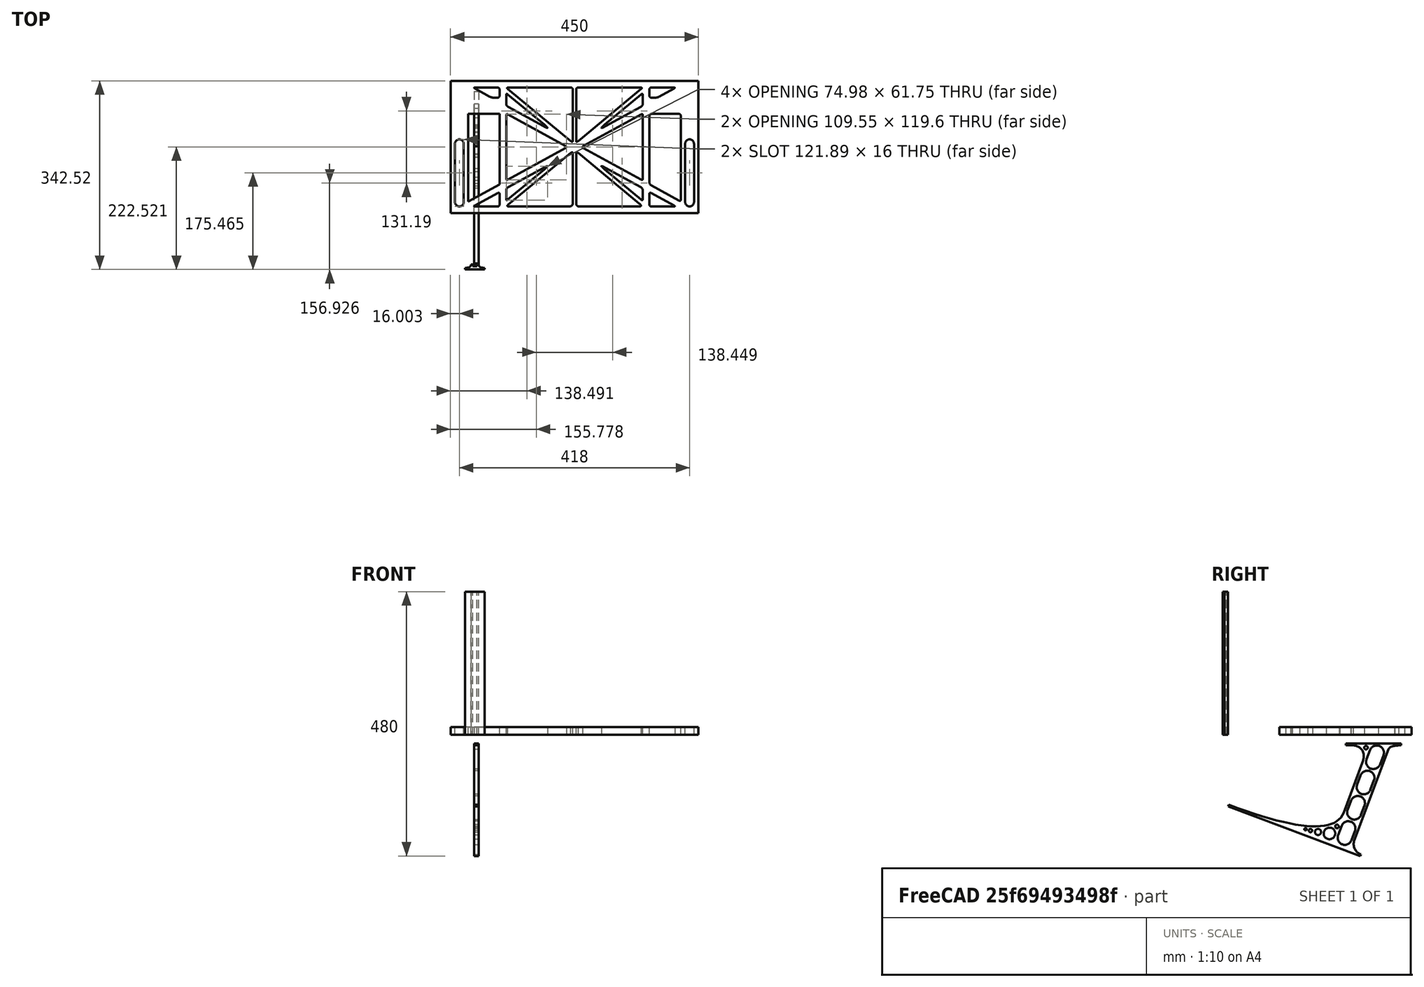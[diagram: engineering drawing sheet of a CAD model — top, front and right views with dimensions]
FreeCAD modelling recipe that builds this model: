
FCSTD DOCUMENT  (FreeCAD 0.19R0.19.2)
Label: laptopStand138FCStd
License: All rights reserved
LicenseURL: http://en.wikipedia.org/wiki/All_rights_reserved
objects: Sketcher::SketchObject×3, Part::Extrusion×3
note: 6 computed .brp shape members not serialized (recipe doc carries the construction recipe); baked Part::Feature solids carry a one-line shape summary decoded from their .brp

FEATURE [Sketcher::SketchObject] Sketch
  FullyConstrained = false
  sketch-geometry (349):
    g0: LineSegment StartX=-10.9272 StartY=-82.7794 StartZ=0 EndX=46.0728 EndY=-51.4823 EndZ=0
    g1: LineSegment StartX=-10.9272 StartY=76.4095 StartZ=0 EndX=-10.9272 EndY=-82.7794 EndZ=0
    g2: LineSegment StartX=46.0728 StartY=76.4095 StartZ=0 EndX=46.0728 EndY=-51.4823 EndZ=0
    g3: LineSegment StartX=-42.9272 StartY=136.221 StartZ=0 EndX=-42.9272 EndY=-103.779 EndZ=0
    g4: LineSegment StartX=407.073 StartY=136.221 StartZ=0 EndX=407.073 EndY=-103.779 EndZ=0
    g5: ArcOfCircle CenterX=-26.9272 CenterY=-83.7794 CenterZ=0 NormalX=0 NormalY=0 NormalZ=1 AngleXU=0 Radius=8 StartAngle=3.14159 EndAngle=6.28319
    g6: ArcOfCircle CenterX=391.073 CenterY=22.1087 CenterZ=0 NormalX=0 NormalY=0 NormalZ=1 AngleXU=0 Radius=8 StartAngle=-4.4e-15 EndAngle=3.14159
    g7: LineSegment StartX=399.073 StartY=22.1087 StartZ=0 EndX=399.073 EndY=-83.7794 EndZ=0
    g8: LineSegment StartX=383.073 StartY=22.1087 StartZ=0 EndX=383.073 EndY=-83.7794 EndZ=0
    g9: ArcOfCircle CenterX=391.073 CenterY=-83.7794 CenterZ=0 NormalX=0 NormalY=0 NormalZ=1 AngleXU=0 Radius=8 StartAngle=3.14159 EndAngle=6.28319
    g10: Circle CenterX=175.022 CenterY=27.0628 CenterZ=0 NormalX=0 NormalY=0 NormalZ=1 AngleXU=0 Radius=1
    g11: Circle CenterX=179.022 CenterY=24.8665 CenterZ=0 NormalX=0 NormalY=0 NormalZ=1 AngleXU=0 Radius=1
    g12: Circle CenterX=179.022 CenterY=27.0628 CenterZ=0 NormalX=0 NormalY=0 NormalZ=1 AngleXU=0 Radius=1
    g13: BSplineCurve PolesCount=3 KnotsCount=2 Degree=2 IsPeriodic=0
    g14: GeomPoint X=175.022 Y=27.0628 Z=0
    g15: GeomPoint X=179.022 Y=27.0628 Z=0
    g16: Circle CenterX=189.124 CenterY=27.0628 CenterZ=0 NormalX=0 NormalY=0 NormalZ=1 AngleXU=0 Radius=1
    g17: Circle CenterX=185.124 CenterY=24.8665 CenterZ=0 NormalX=0 NormalY=0 NormalZ=1 AngleXU=0 Radius=1
    g18: Circle CenterX=185.124 CenterY=27.0628 CenterZ=0 NormalX=0 NormalY=0 NormalZ=1 AngleXU=0 Radius=1
    g19: BSplineCurve PolesCount=3 KnotsCount=2 Degree=2 IsPeriodic=0
    g20: GeomPoint X=189.124 Y=27.0628 Z=0
    g21: GeomPoint X=185.124 Y=27.0628 Z=0
    g22: Circle CenterX=175.022 CenterY=5.37834 CenterZ=0 NormalX=0 NormalY=0 NormalZ=1 AngleXU=0 Radius=1
    g23: Circle CenterX=179.022 CenterY=7.57463 CenterZ=0 NormalX=0 NormalY=0 NormalZ=1 AngleXU=0 Radius=1
    g24: Circle CenterX=179.022 CenterY=5.34704 CenterZ=0 NormalX=0 NormalY=0 NormalZ=1 AngleXU=0 Radius=1
    g25: BSplineCurve PolesCount=3 KnotsCount=2 Degree=2 IsPeriodic=0
    g26: GeomPoint X=175.022 Y=5.37834 Z=0
    g27: GeomPoint X=179.022 Y=5.34704 Z=0
    g28: Circle CenterX=189.124 CenterY=5.37834 CenterZ=0 NormalX=0 NormalY=0 NormalZ=1 AngleXU=0 Radius=1
    g29: Circle CenterX=185.124 CenterY=7.57463 CenterZ=0 NormalX=0 NormalY=0 NormalZ=1 AngleXU=0 Radius=1
    g30: Circle CenterX=185.124 CenterY=5.34704 CenterZ=0 NormalX=0 NormalY=0 NormalZ=1 AngleXU=0 Radius=1
    g31: BSplineCurve PolesCount=3 KnotsCount=2 Degree=2 IsPeriodic=0
    g32: GeomPoint X=189.124 Y=5.37834 Z=0
    g33: GeomPoint X=185.124 Y=5.34704 Z=0
    g34: Circle CenterX=165.871 CenterY=18.1458 CenterZ=0 NormalX=0 NormalY=0 NormalZ=1 AngleXU=0 Radius=1
    g35: Circle CenterX=169.377 CenterY=16.2206 CenterZ=0 NormalX=0 NormalY=0 NormalZ=1 AngleXU=0 Radius=1
    g36: Circle CenterX=165.871 CenterY=14.2954 CenterZ=0 NormalX=0 NormalY=0 NormalZ=1 AngleXU=0 Radius=1
    g37: BSplineCurve PolesCount=3 KnotsCount=2 Degree=2 IsPeriodic=0
    g38: GeomPoint X=165.871 Y=18.1458 Z=0
    g39: GeomPoint X=165.871 Y=14.2954 Z=0
    g40: Circle CenterX=198.275 CenterY=18.1458 CenterZ=0 NormalX=0 NormalY=0 NormalZ=1 AngleXU=0 Radius=1
    g41: Circle CenterX=194.768 CenterY=16.2206 CenterZ=0 NormalX=0 NormalY=0 NormalZ=1 AngleXU=0 Radius=1
    g42: Circle CenterX=198.275 CenterY=14.2954 CenterZ=0 NormalX=0 NormalY=0 NormalZ=1 AngleXU=0 Radius=1
    g43: BSplineCurve PolesCount=3 KnotsCount=2 Degree=2 IsPeriodic=0
    g44: GeomPoint X=198.275 Y=18.1458 Z=0
    g45: GeomPoint X=198.275 Y=14.2954 Z=0
    g46: LineSegment StartX=407.073 StartY=-103.779 StartZ=0 EndX=-42.9272 EndY=-103.779 EndZ=0
    g47: LineSegment StartX=407.073 StartY=136.221 StartZ=0 EndX=-42.9272 EndY=136.221 EndZ=0
    g48: LineSegment StartX=46.0728 StartY=76.4095 StartZ=0 EndX=-10.9272 EndY=76.4095 EndZ=0
    g49: Circle CenterX=125.607 CenterY=54.1951 CenterZ=0 NormalX=0 NormalY=0 NormalZ=1 AngleXU=0 Radius=1
    g50: Circle CenterX=139.632 CenterY=46.4944 CenterZ=0 NormalX=0 NormalY=0 NormalZ=1 AngleXU=0 Radius=1
    g51: Circle CenterX=127.326 CenterY=56.7187 CenterZ=0 NormalX=0 NormalY=0 NormalZ=1 AngleXU=0 Radius=1
    g52: BSplineCurve PolesCount=3 KnotsCount=2 Degree=2 IsPeriodic=0
    g53: GeomPoint X=125.607 Y=54.1951 Z=0
    g54: GeomPoint X=127.326 Y=56.7187 Z=0
    g55: Circle CenterX=236.821 CenterY=56.7187 CenterZ=0 NormalX=0 NormalY=0 NormalZ=1 AngleXU=0 Radius=1
    g56: Circle CenterX=224.513 CenterY=46.4944 CenterZ=0 NormalX=0 NormalY=0 NormalZ=1 AngleXU=0 Radius=1
    g57: Circle CenterX=238.538 CenterY=54.1951 CenterZ=0 NormalX=0 NormalY=0 NormalZ=1 AngleXU=0 Radius=1
    g58: BSplineCurve PolesCount=3 KnotsCount=2 Degree=2 IsPeriodic=0
    g59: GeomPoint X=236.821 Y=56.7187 Z=0
    g60: GeomPoint X=238.538 Y=54.1951 Z=0
    g61: Circle CenterX=238.538 CenterY=-21.7539 CenterZ=0 NormalX=0 NormalY=0 NormalZ=1 AngleXU=0 Radius=1
    g62: Circle CenterX=224.513 CenterY=-14.0532 CenterZ=0 NormalX=0 NormalY=0 NormalZ=1 AngleXU=0 Radius=1
    g63: Circle CenterX=236.821 CenterY=-24.2775 CenterZ=0 NormalX=0 NormalY=0 NormalZ=1 AngleXU=0 Radius=1
    g64: BSplineCurve PolesCount=3 KnotsCount=2 Degree=2 IsPeriodic=0
    g65: GeomPoint X=238.538 Y=-21.7539 Z=0
    g66: GeomPoint X=236.821 Y=-24.2775 Z=0
    g67: Circle CenterX=125.607 CenterY=-21.7539 CenterZ=0 NormalX=0 NormalY=0 NormalZ=1 AngleXU=0 Radius=1
    g68: Circle CenterX=139.632 CenterY=-14.0532 CenterZ=0 NormalX=0 NormalY=0 NormalZ=1 AngleXU=0 Radius=1
    g69: Circle CenterX=127.325 CenterY=-24.2775 CenterZ=0 NormalX=0 NormalY=0 NormalZ=1 AngleXU=0 Radius=1
    g70: BSplineCurve PolesCount=3 KnotsCount=2 Degree=2 IsPeriodic=0
    g71: GeomPoint X=125.607 Y=-21.7539 Z=0
    g72: GeomPoint X=127.325 Y=-24.2775 Z=0
    g73: Circle CenterX=302.996 CenterY=111.695 CenterZ=0 NormalX=0 NormalY=0 NormalZ=1 AngleXU=0 Radius=1
    g74: Circle CenterX=306.073 CenterY=114.251 CenterZ=0 NormalX=0 NormalY=0 NormalZ=1 AngleXU=0 Radius=1
    g75: Circle CenterX=306.073 CenterY=110.251 CenterZ=0 NormalX=0 NormalY=0 NormalZ=1 AngleXU=0 Radius=1
    g76: BSplineCurve PolesCount=3 KnotsCount=2 Degree=2 IsPeriodic=0
    g77: GeomPoint X=302.996 Y=111.695 Z=0
    g78: GeomPoint X=306.073 Y=110.251 Z=0
    g79: Circle CenterX=306.073 CenterY=95.2763 CenterZ=0 NormalX=0 NormalY=0 NormalZ=1 AngleXU=0 Radius=1
    g80: Circle CenterX=306.073 CenterY=91.2763 CenterZ=0 NormalX=0 NormalY=0 NormalZ=1 AngleXU=0 Radius=1
    g81: Circle CenterX=302.567 CenterY=89.3511 CenterZ=0 NormalX=0 NormalY=0 NormalZ=1 AngleXU=0 Radius=1
    g82: BSplineCurve PolesCount=3 KnotsCount=2 Degree=2 IsPeriodic=0
    g83: GeomPoint X=306.073 Y=95.2763 Z=0
    g84: GeomPoint X=302.567 Y=89.3511 Z=0
    g85: LineSegment StartX=306.073 StartY=110.251 StartZ=0 EndX=306.073 EndY=95.2763 EndZ=0
    g86: LineSegment StartX=302.996 StartY=111.695 StartZ=0 EndX=236.821 EndY=56.7187 EndZ=0
    g87: LineSegment StartX=238.538 StartY=54.1951 StartZ=0 EndX=302.567 EndY=89.3511 EndZ=0
    g88: Circle CenterX=61.1496 CenterY=111.695 CenterZ=0 NormalX=0 NormalY=0 NormalZ=1 AngleXU=0 Radius=1
    g89: Circle CenterX=58.0728 CenterY=114.251 CenterZ=0 NormalX=0 NormalY=0 NormalZ=1 AngleXU=0 Radius=1
    g90: Circle CenterX=58.0728 CenterY=110.251 CenterZ=0 NormalX=0 NormalY=0 NormalZ=1 AngleXU=0 Radius=1
    g91: BSplineCurve PolesCount=3 KnotsCount=2 Degree=2 IsPeriodic=0
    g92: GeomPoint X=61.1496 Y=111.695 Z=0
    g93: GeomPoint X=58.0728 Y=110.251 Z=0
    g94: Circle CenterX=61.5791 CenterY=89.3511 CenterZ=0 NormalX=0 NormalY=0 NormalZ=1 AngleXU=0 Radius=1
    g95: Circle CenterX=58.0728 CenterY=91.2763 CenterZ=0 NormalX=0 NormalY=0 NormalZ=1 AngleXU=0 Radius=1
    g96: Circle CenterX=58.0728 CenterY=95.2763 CenterZ=0 NormalX=0 NormalY=0 NormalZ=1 AngleXU=0 Radius=1
    g97: BSplineCurve PolesCount=3 KnotsCount=2 Degree=2 IsPeriodic=0
    g98: GeomPoint X=61.5791 Y=89.3511 Z=0
    g99: GeomPoint X=58.0728 Y=95.2763 Z=0
    g100: LineSegment StartX=58.0728 StartY=110.251 StartZ=0 EndX=58.0728 EndY=95.2763 EndZ=0
    g101: LineSegment StartX=61.1496 StartY=111.695 StartZ=0 EndX=127.326 EndY=56.7187 EndZ=0
    g102: LineSegment StartX=125.607 StartY=54.1951 StartZ=0 EndX=61.5791 EndY=89.3511 EndZ=0
    g103: Circle CenterX=61.5791 CenterY=-56.9099 CenterZ=0 NormalX=0 NormalY=0 NormalZ=1 AngleXU=0 Radius=1
    g104: Circle CenterX=58.0728 CenterY=-58.8351 CenterZ=0 NormalX=0 NormalY=0 NormalZ=1 AngleXU=0 Radius=1
    g105: Circle CenterX=58.0728 CenterY=-62.8351 CenterZ=0 NormalX=0 NormalY=0 NormalZ=1 AngleXU=0 Radius=1
    g106: BSplineCurve PolesCount=3 KnotsCount=2 Degree=2 IsPeriodic=0
    g107: GeomPoint X=61.5791 Y=-56.9099 Z=0
    g108: GeomPoint X=58.0728 Y=-62.8351 Z=0
    g109: Circle CenterX=58.0728 CenterY=-77.8102 CenterZ=0 NormalX=0 NormalY=0 NormalZ=1 AngleXU=0 Radius=1
    g110: Circle CenterX=58.0728 CenterY=-81.8102 CenterZ=0 NormalX=0 NormalY=0 NormalZ=1 AngleXU=0 Radius=1
    g111: Circle CenterX=61.1496 CenterY=-79.2541 CenterZ=0 NormalX=0 NormalY=0 NormalZ=1 AngleXU=0 Radius=1
    g112: BSplineCurve PolesCount=3 KnotsCount=2 Degree=2 IsPeriodic=0
    g113: GeomPoint X=58.0728 Y=-77.8102 Z=0
    g114: GeomPoint X=61.1496 Y=-79.2541 Z=0
    g115: LineSegment StartX=58.0728 StartY=-62.8351 StartZ=0 EndX=58.0728 EndY=-77.8102 EndZ=0
    g116: LineSegment StartX=61.1496 StartY=-79.2541 StartZ=0 EndX=127.325 EndY=-24.2775 EndZ=0
    g117: LineSegment StartX=125.607 StartY=-21.7539 StartZ=0 EndX=61.5791 EndY=-56.9099 EndZ=0
    g118: Circle CenterX=302.567 CenterY=-56.9099 CenterZ=0 NormalX=0 NormalY=0 NormalZ=1 AngleXU=0 Radius=1
    g119: Circle CenterX=306.073 CenterY=-58.8351 CenterZ=0 NormalX=0 NormalY=0 NormalZ=1 AngleXU=0 Radius=1
    g120: Circle CenterX=306.073 CenterY=-62.8351 CenterZ=0 NormalX=0 NormalY=0 NormalZ=1 AngleXU=0 Radius=1
    g121: BSplineCurve PolesCount=3 KnotsCount=2 Degree=2 IsPeriodic=0
    g122: GeomPoint X=302.567 Y=-56.9099 Z=0
    g123: GeomPoint X=306.073 Y=-62.8351 Z=0
    g124: Circle CenterX=302.996 CenterY=-79.2541 CenterZ=0 NormalX=0 NormalY=0 NormalZ=1 AngleXU=0 Radius=1
    g125: Circle CenterX=306.073 CenterY=-81.8102 CenterZ=0 NormalX=0 NormalY=0 NormalZ=1 AngleXU=0 Radius=1
    g126: Circle CenterX=306.073 CenterY=-77.8102 CenterZ=0 NormalX=0 NormalY=0 NormalZ=1 AngleXU=0 Radius=1
    g127: BSplineCurve PolesCount=3 KnotsCount=2 Degree=2 IsPeriodic=0
    g128: GeomPoint X=302.996 Y=-79.2541 Z=0
    g129: GeomPoint X=306.073 Y=-77.8102 Z=0
    g130: LineSegment StartX=306.073 StartY=-62.8351 StartZ=0 EndX=306.073 EndY=-77.8102 EndZ=0
    g131: LineSegment StartX=302.996 StartY=-79.2541 StartZ=0 EndX=236.821 EndY=-24.2775 EndZ=0
    g132: LineSegment StartX=238.538 StartY=-21.7539 StartZ=0 EndX=302.567 EndY=-56.9099 EndZ=0
    g133: Circle CenterX=61.6457 CenterY=-88.8112 CenterZ=0 NormalX=0 NormalY=0 NormalZ=1 AngleXU=0 Radius=1
    g134: Circle CenterX=58.0728 CenterY=-91.7794 CenterZ=0 NormalX=0 NormalY=0 NormalZ=1 AngleXU=0 Radius=1
    g135: Circle CenterX=63.9135 CenterY=-91.7794 CenterZ=0 NormalX=0 NormalY=0 NormalZ=1 AngleXU=0 Radius=1
    g136: BSplineCurve PolesCount=3 KnotsCount=2 Degree=2 IsPeriodic=0
    g137: GeomPoint X=61.6457 Y=-88.8112 Z=0
    g138: GeomPoint X=63.9135 Y=-91.7794 Z=0
    g139: Circle CenterX=179.022 CenterY=-85.8163 CenterZ=0 NormalX=0 NormalY=0 NormalZ=1 AngleXU=0 Radius=1
    g140: Circle CenterX=179.022 CenterY=-91.7794 CenterZ=0 NormalX=0 NormalY=0 NormalZ=1 AngleXU=0 Radius=1
    g141: Circle CenterX=171.895 CenterY=-91.7794 CenterZ=0 NormalX=0 NormalY=0 NormalZ=1 AngleXU=0 Radius=1
    g142: BSplineCurve PolesCount=3 KnotsCount=2 Degree=2 IsPeriodic=0
    g143: GeomPoint X=179.022 Y=-85.8163 Z=0
    g144: GeomPoint X=171.895 Y=-91.7794 Z=0
    g145: Circle CenterX=185.124 CenterY=-86.2028 CenterZ=0 NormalX=0 NormalY=0 NormalZ=1 AngleXU=0 Radius=1
    g146: Circle CenterX=185.124 CenterY=-91.7794 CenterZ=0 NormalX=0 NormalY=0 NormalZ=1 AngleXU=0 Radius=1
    g147: Circle CenterX=191.747 CenterY=-91.7794 CenterZ=0 NormalX=0 NormalY=0 NormalZ=1 AngleXU=0 Radius=1
    g148: BSplineCurve PolesCount=3 KnotsCount=2 Degree=2 IsPeriodic=0
    g149: GeomPoint X=185.124 Y=-86.2028 Z=0
    g150: GeomPoint X=191.747 Y=-91.7794 Z=0
    g151: Circle CenterX=299.888 CenterY=-86.6413 CenterZ=0 NormalX=0 NormalY=0 NormalZ=1 AngleXU=0 Radius=1
    g152: Circle CenterX=306.073 CenterY=-91.7794 CenterZ=0 NormalX=0 NormalY=0 NormalZ=1 AngleXU=0 Radius=1
    g153: Circle CenterX=298.776 CenterY=-91.7794 CenterZ=0 NormalX=0 NormalY=0 NormalZ=1 AngleXU=0 Radius=1
    g154: BSplineCurve PolesCount=3 KnotsCount=2 Degree=2 IsPeriodic=0
    g155: GeomPoint X=299.888 Y=-86.6413 Z=0
    g156: GeomPoint X=298.776 Y=-91.7794 Z=0
    g157: LineSegment StartX=189.124 StartY=5.37834 StartZ=0 EndX=299.888 EndY=-86.6413 EndZ=0
    g158: LineSegment StartX=298.776 StartY=-91.7794 StartZ=0 EndX=191.747 EndY=-91.7794 EndZ=0
    g159: LineSegment StartX=185.124 StartY=-86.2028 StartZ=0 EndX=185.124 EndY=5.34704 EndZ=0
    g160: LineSegment StartX=179.022 StartY=5.34704 StartZ=0 EndX=179.022 EndY=-85.8163 EndZ=0
    g161: LineSegment StartX=171.895 StartY=-91.7794 StartZ=0 EndX=63.9135 EndY=-91.7794 EndZ=0
    g162: LineSegment StartX=61.6457 StartY=-88.8112 StartZ=0 EndX=175.022 EndY=5.37834 EndZ=0
    g163: Circle CenterX=302.073 CenterY=124.221 CenterZ=0 NormalX=0 NormalY=0 NormalZ=1 AngleXU=0 Radius=1
    g164: Circle CenterX=306.073 CenterY=124.221 CenterZ=0 NormalX=0 NormalY=0 NormalZ=1 AngleXU=0 Radius=1
    g165: Circle CenterX=302.996 CenterY=121.665 CenterZ=0 NormalX=0 NormalY=0 NormalZ=1 AngleXU=0 Radius=1
    g166: BSplineCurve PolesCount=3 KnotsCount=2 Degree=2 IsPeriodic=0
    g167: GeomPoint X=302.073 Y=124.221 Z=0
    g168: GeomPoint X=302.996 Y=121.665 Z=0
    g169: Circle CenterX=189.124 CenterY=124.221 CenterZ=0 NormalX=0 NormalY=0 NormalZ=1 AngleXU=0 Radius=1
    g170: Circle CenterX=185.124 CenterY=124.221 CenterZ=0 NormalX=0 NormalY=0 NormalZ=1 AngleXU=0 Radius=1
    g171: Circle CenterX=185.124 CenterY=120.221 CenterZ=0 NormalX=0 NormalY=0 NormalZ=1 AngleXU=0 Radius=1
    g172: BSplineCurve PolesCount=3 KnotsCount=2 Degree=2 IsPeriodic=0
    g173: GeomPoint X=189.124 Y=124.221 Z=0
    g174: GeomPoint X=185.124 Y=120.221 Z=0
    g175: Circle CenterX=175.022 CenterY=124.221 CenterZ=0 NormalX=0 NormalY=0 NormalZ=1 AngleXU=0 Radius=1
    g176: Circle CenterX=179.022 CenterY=124.221 CenterZ=0 NormalX=0 NormalY=0 NormalZ=1 AngleXU=0 Radius=1
    g177: Circle CenterX=179.022 CenterY=120.221 CenterZ=0 NormalX=0 NormalY=0 NormalZ=1 AngleXU=0 Radius=1
    g178: BSplineCurve PolesCount=3 KnotsCount=2 Degree=2 IsPeriodic=0
    g179: GeomPoint X=175.022 Y=124.221 Z=0
    g180: GeomPoint X=179.022 Y=120.221 Z=0
    g181: Circle CenterX=62.0728 CenterY=124.221 CenterZ=0 NormalX=0 NormalY=0 NormalZ=1 AngleXU=0 Radius=1
    g182: Circle CenterX=58.0728 CenterY=124.221 CenterZ=0 NormalX=0 NormalY=0 NormalZ=1 AngleXU=0 Radius=1
    g183: Circle CenterX=61.1496 CenterY=121.665 CenterZ=0 NormalX=0 NormalY=0 NormalZ=1 AngleXU=0 Radius=1
    g184: BSplineCurve PolesCount=3 KnotsCount=2 Degree=2 IsPeriodic=0
    g185: GeomPoint X=62.0728 Y=124.221 Z=0
    g186: GeomPoint X=61.1496 Y=121.665 Z=0
    g187: LineSegment StartX=62.0728 StartY=124.221 StartZ=0 EndX=175.022 EndY=124.221 EndZ=0
    g188: LineSegment StartX=179.022 StartY=120.221 StartZ=0 EndX=179.022 EndY=27.0628 EndZ=0
    g189: LineSegment StartX=185.124 StartY=27.0628 StartZ=0 EndX=185.124 EndY=120.221 EndZ=0
    g190: LineSegment StartX=189.124 StartY=124.221 StartZ=0 EndX=302.073 EndY=124.221 EndZ=0
    g191: LineSegment StartX=302.996 StartY=121.665 StartZ=0 EndX=189.124 EndY=27.0628 EndZ=0
    g192: LineSegment StartX=175.022 StartY=27.0628 StartZ=0 EndX=61.1496 EndY=121.665 EndZ=0
    g193: Circle CenterX=61.5791 CenterY=75.4095 CenterZ=0 NormalX=0 NormalY=0 NormalZ=1 AngleXU=0 Radius=1
    g194: Circle CenterX=58.0728 CenterY=77.3346 CenterZ=0 NormalX=0 NormalY=0 NormalZ=1 AngleXU=0 Radius=1
    g195: Circle CenterX=58.0728 CenterY=73.3346 CenterZ=0 NormalX=0 NormalY=0 NormalZ=1 AngleXU=0 Radius=1
    g196: BSplineCurve PolesCount=3 KnotsCount=2 Degree=2 IsPeriodic=0
    g197: GeomPoint X=61.5791 Y=75.4095 Z=0
    g198: GeomPoint X=58.0728 Y=73.3346 Z=0
    g199: Circle CenterX=58.0728 CenterY=-40.8935 CenterZ=0 NormalX=0 NormalY=0 NormalZ=1 AngleXU=0 Radius=1
    g200: Circle CenterX=58.0728 CenterY=-44.8935 CenterZ=0 NormalX=0 NormalY=0 NormalZ=1 AngleXU=0 Radius=1
    g201: Circle CenterX=61.5791 CenterY=-42.9683 CenterZ=0 NormalX=0 NormalY=0 NormalZ=1 AngleXU=0 Radius=1
    g202: BSplineCurve PolesCount=3 KnotsCount=2 Degree=2 IsPeriodic=0
    g203: GeomPoint X=58.0728 Y=-40.8935 Z=0
    g204: GeomPoint X=61.5791 Y=-42.9683 Z=0
    g205: LineSegment StartX=61.5791 StartY=-42.9683 StartZ=0 EndX=165.871 EndY=14.2954 EndZ=0
    g206: LineSegment StartX=165.871 StartY=18.1458 StartZ=0 EndX=61.5791 EndY=75.4095 EndZ=0
    g207: LineSegment StartX=58.0728 StartY=73.3346 StartZ=0 EndX=58.0728 EndY=-40.8935 EndZ=0
    g208: Circle CenterX=302.567 CenterY=-42.9683 CenterZ=0 NormalX=0 NormalY=0 NormalZ=1 AngleXU=0 Radius=1
    g209: Circle CenterX=306.073 CenterY=-44.8935 CenterZ=0 NormalX=0 NormalY=0 NormalZ=1 AngleXU=0 Radius=1
    g210: Circle CenterX=306.073 CenterY=-40.8935 CenterZ=0 NormalX=0 NormalY=0 NormalZ=1 AngleXU=0 Radius=1
    g211: BSplineCurve PolesCount=3 KnotsCount=2 Degree=2 IsPeriodic=0
    g212: GeomPoint X=302.567 Y=-42.9683 Z=0
    g213: GeomPoint X=306.073 Y=-40.8935 Z=0
    g214: Circle CenterX=306.073 CenterY=73.3346 CenterZ=0 NormalX=0 NormalY=0 NormalZ=1 AngleXU=0 Radius=1
    g215: Circle CenterX=306.073 CenterY=77.3346 CenterZ=0 NormalX=0 NormalY=0 NormalZ=1 AngleXU=0 Radius=1
    g216: Circle CenterX=302.567 CenterY=75.4095 CenterZ=0 NormalX=0 NormalY=0 NormalZ=1 AngleXU=0 Radius=1
    g217: BSplineCurve PolesCount=3 KnotsCount=2 Degree=2 IsPeriodic=0
    g218: GeomPoint X=306.073 Y=73.3346 Z=0
    g219: GeomPoint X=302.567 Y=75.4095 Z=0
    g220: LineSegment StartX=302.567 StartY=-42.9683 StartZ=0 EndX=198.275 EndY=14.2954 EndZ=0
    g221: LineSegment StartX=198.275 StartY=18.1458 StartZ=0 EndX=302.567 EndY=75.4095 EndZ=0
    g222: LineSegment StartX=306.073 StartY=73.3346 StartZ=0 EndX=306.073 EndY=-40.8935 EndZ=0
    g223: LineSegment StartX=322.073 StartY=105.865 StartZ=0 EndX=328.643 EndY=105.865 EndZ=0
    g224: LineSegment StartX=318.073 StartY=120.221 StartZ=0 EndX=318.073 EndY=109.865 EndZ=0
    g225: LineSegment StartX=336.157 StartY=107.779 StartZ=0 EndX=362.567 EndY=122.294 EndZ=0
    g226: Circle CenterX=362.073 CenterY=124.221 CenterZ=0 NormalX=0 NormalY=0 NormalZ=1 AngleXU=0 Radius=1
    g227: Circle CenterX=366.073 CenterY=124.221 CenterZ=0 NormalX=0 NormalY=0 NormalZ=1 AngleXU=0 Radius=1
    g228: Circle CenterX=362.567 CenterY=122.294 CenterZ=0 NormalX=0 NormalY=0 NormalZ=1 AngleXU=0 Radius=1
    g229: BSplineCurve PolesCount=3 KnotsCount=2 Degree=2 IsPeriodic=0
    g230: GeomPoint X=362.073 Y=124.221 Z=0
    g231: GeomPoint X=362.567 Y=122.294 Z=0
    g232: Circle CenterX=322.073 CenterY=124.221 CenterZ=0 NormalX=0 NormalY=0 NormalZ=1 AngleXU=0 Radius=1
    g233: Circle CenterX=318.073 CenterY=124.221 CenterZ=0 NormalX=0 NormalY=0 NormalZ=1 AngleXU=0 Radius=1
    g234: Circle CenterX=318.073 CenterY=120.221 CenterZ=0 NormalX=0 NormalY=0 NormalZ=1 AngleXU=0 Radius=1
    g235: BSplineCurve PolesCount=3 KnotsCount=2 Degree=2 IsPeriodic=0
    g236: GeomPoint X=322.073 Y=124.221 Z=0
    g237: GeomPoint X=318.073 Y=120.221 Z=0
    g238: Circle CenterX=322.073 CenterY=105.865 CenterZ=0 NormalX=0 NormalY=0 NormalZ=1 AngleXU=0 Radius=1
    g239: Circle CenterX=318.073 CenterY=105.865 CenterZ=0 NormalX=0 NormalY=0 NormalZ=1 AngleXU=0 Radius=1
    g240: Circle CenterX=318.073 CenterY=109.865 CenterZ=0 NormalX=0 NormalY=0 NormalZ=1 AngleXU=0 Radius=1
    g241: BSplineCurve PolesCount=3 KnotsCount=2 Degree=2 IsPeriodic=0
    g242: GeomPoint X=322.073 Y=105.865 Z=0
    g243: GeomPoint X=318.073 Y=109.865 Z=0
    g244: Circle CenterX=336.157 CenterY=107.779 CenterZ=0 NormalX=0 NormalY=0 NormalZ=1 AngleXU=0 Radius=1
    g245: Circle CenterX=332.651 CenterY=105.853 CenterZ=0 NormalX=0 NormalY=0 NormalZ=1 AngleXU=0 Radius=1
    g246: Circle CenterX=328.643 CenterY=105.865 CenterZ=0 NormalX=0 NormalY=0 NormalZ=1 AngleXU=0 Radius=1
    g247: BSplineCurve PolesCount=3 KnotsCount=2 Degree=2 IsPeriodic=0
    g248: GeomPoint X=336.157 Y=107.779 Z=0
    g249: GeomPoint X=328.643 Y=105.865 Z=0
    g250: LineSegment StartX=322.073 StartY=124.221 StartZ=0 EndX=362.073 EndY=124.221 EndZ=0
    g251: Circle CenterX=371.567 CenterY=-80.8644 CenterZ=0 NormalX=0 NormalY=0 NormalZ=1 AngleXU=0 Radius=1
    g252: Circle CenterX=375.073 CenterY=-82.7896 CenterZ=0 NormalX=0 NormalY=0 NormalZ=1 AngleXU=0 Radius=1
    g253: Circle CenterX=375.073 CenterY=-78.7896 CenterZ=0 NormalX=0 NormalY=0 NormalZ=1 AngleXU=0 Radius=1
    g254: BSplineCurve PolesCount=3 KnotsCount=2 Degree=2 IsPeriodic=0
    g255: GeomPoint X=371.567 Y=-80.8644 Z=0
    g256: GeomPoint X=375.073 Y=-78.7896 Z=0
    g257: Circle CenterX=321.579 CenterY=-53.4075 CenterZ=0 NormalX=0 NormalY=0 NormalZ=1 AngleXU=0 Radius=1
    g258: Circle CenterX=318.073 CenterY=-51.4823 CenterZ=0 NormalX=0 NormalY=0 NormalZ=1 AngleXU=0 Radius=1
    g259: Circle CenterX=318.073 CenterY=-47.4805 CenterZ=0 NormalX=0 NormalY=0 NormalZ=1 AngleXU=0 Radius=1
    g260: BSplineCurve PolesCount=3 KnotsCount=2 Degree=2 IsPeriodic=0
    g261: GeomPoint X=321.579 Y=-53.4075 Z=0
    g262: GeomPoint X=318.073 Y=-47.4805 Z=0
    g263: LineSegment StartX=371.567 StartY=-80.8644 StartZ=0 EndX=321.579 EndY=-53.4075 EndZ=0
    g264: Circle CenterX=321.579 CenterY=-67.3492 CenterZ=0 NormalX=0 NormalY=0 NormalZ=1 AngleXU=0 Radius=1
    g265: Circle CenterX=318.073 CenterY=-65.424 CenterZ=0 NormalX=0 NormalY=0 NormalZ=1 AngleXU=0 Radius=1
    g266: Circle CenterX=318.073 CenterY=-69.424 CenterZ=0 NormalX=0 NormalY=0 NormalZ=1 AngleXU=0 Radius=1
    g267: BSplineCurve PolesCount=3 KnotsCount=2 Degree=2 IsPeriodic=0
    g268: GeomPoint X=321.579 Y=-67.3492 Z=0
    g269: GeomPoint X=318.073 Y=-69.424 Z=0
    g270: Circle CenterX=362.567 CenterY=-89.8542 CenterZ=0 NormalX=0 NormalY=0 NormalZ=1 AngleXU=0 Radius=1
    g271: Circle CenterX=366.073 CenterY=-91.7794 CenterZ=0 NormalX=0 NormalY=0 NormalZ=1 AngleXU=0 Radius=1
    g272: Circle CenterX=362.073 CenterY=-91.7794 CenterZ=0 NormalX=0 NormalY=0 NormalZ=1 AngleXU=0 Radius=1
    g273: BSplineCurve PolesCount=3 KnotsCount=2 Degree=2 IsPeriodic=0
    g274: GeomPoint X=362.567 Y=-89.8542 Z=0
    g275: GeomPoint X=362.073 Y=-91.7794 Z=0
    g276: Circle CenterX=322.073 CenterY=-91.7794 CenterZ=0 NormalX=0 NormalY=0 NormalZ=1 AngleXU=0 Radius=1
    g277: Circle CenterX=318.073 CenterY=-91.7794 CenterZ=0 NormalX=0 NormalY=0 NormalZ=1 AngleXU=0 Radius=1
    g278: Circle CenterX=318.073 CenterY=-87.7794 CenterZ=0 NormalX=0 NormalY=0 NormalZ=1 AngleXU=0 Radius=1
    g279: BSplineCurve PolesCount=3 KnotsCount=2 Degree=2 IsPeriodic=0
    g280: GeomPoint X=322.073 Y=-91.7794 Z=0
    g281: GeomPoint X=318.073 Y=-87.7794 Z=0
    g282: LineSegment StartX=362.567 StartY=-89.8542 StartZ=0 EndX=321.579 EndY=-67.3492 EndZ=0
    g283: LineSegment StartX=318.073 StartY=-69.424 StartZ=0 EndX=318.073 EndY=-87.7794 EndZ=0
    g284: LineSegment StartX=322.073 StartY=-91.7794 StartZ=0 EndX=362.073 EndY=-91.7794 EndZ=0
    g285: Circle CenterX=2.07281 CenterY=124.221 CenterZ=0 NormalX=0 NormalY=0 NormalZ=1 AngleXU=0 Radius=1
    g286: Circle CenterX=1.57905 CenterY=122.295 CenterZ=0 NormalX=0 NormalY=0 NormalZ=1 AngleXU=0 Radius=1
    g287: BSplineCurve PolesCount=3 KnotsCount=2 Degree=2 IsPeriodic=0
    g288: GeomPoint X=2.07281 Y=124.221 Z=0
    g289: GeomPoint X=1.57905 Y=122.295 Z=0
    g290: Circle CenterX=42.0728 CenterY=124.221 CenterZ=0 NormalX=0 NormalY=0 NormalZ=1 AngleXU=0 Radius=1
    g291: Circle CenterX=46.0728 CenterY=124.221 CenterZ=0 NormalX=0 NormalY=0 NormalZ=1 AngleXU=0 Radius=1
    g292: Circle CenterX=46.0728 CenterY=120.221 CenterZ=0 NormalX=0 NormalY=0 NormalZ=1 AngleXU=0 Radius=1
    g293: BSplineCurve PolesCount=3 KnotsCount=2 Degree=2 IsPeriodic=0
    g294: GeomPoint X=42.0728 Y=124.221 Z=0
    g295: GeomPoint X=46.0728 Y=120.221 Z=0
    g296: Circle CenterX=46.0728 CenterY=109.865 CenterZ=0 NormalX=0 NormalY=0 NormalZ=1 AngleXU=0 Radius=1
    g297: Circle CenterX=46.0728 CenterY=105.865 CenterZ=0 NormalX=0 NormalY=0 NormalZ=1 AngleXU=0 Radius=1
    g298: Circle CenterX=42.0728 CenterY=105.865 CenterZ=0 NormalX=0 NormalY=0 NormalZ=1 AngleXU=0 Radius=1
    g299: BSplineCurve PolesCount=3 KnotsCount=2 Degree=2 IsPeriodic=0
    g300: GeomPoint X=46.0728 Y=109.865 Z=0
    g301: GeomPoint X=42.0728 Y=105.865 Z=0
    g302: Circle CenterX=35.5028 CenterY=105.865 CenterZ=0 NormalX=0 NormalY=0 NormalZ=1 AngleXU=0 Radius=1
    g303: Circle CenterX=31.5028 CenterY=105.865 CenterZ=0 NormalX=0 NormalY=0 NormalZ=1 AngleXU=0 Radius=1
    g304: Circle CenterX=27.9965 CenterY=107.79 CenterZ=0 NormalX=0 NormalY=0 NormalZ=1 AngleXU=0 Radius=1
    g305: BSplineCurve PolesCount=3 KnotsCount=2 Degree=2 IsPeriodic=0
    g306: GeomPoint X=35.5028 Y=105.865 Z=0
    g307: GeomPoint X=27.9965 Y=107.79 Z=0
    g308: LineSegment StartX=2.07281 StartY=124.221 StartZ=0 EndX=42.0728 EndY=124.221 EndZ=0
    g309: LineSegment StartX=46.0728 StartY=120.221 StartZ=0 EndX=46.0728 EndY=109.865 EndZ=0
    g310: LineSegment StartX=42.0728 StartY=105.865 StartZ=0 EndX=35.5028 EndY=105.865 EndZ=0
    g311: LineSegment StartX=27.9965 StartY=107.79 StartZ=0 EndX=1.57905 EndY=122.295 EndZ=0
    g312: Circle CenterX=42.5666 CenterY=-67.3492 CenterZ=0 NormalX=0 NormalY=0 NormalZ=1 AngleXU=0 Radius=1
    g313: Circle CenterX=46.0728 CenterY=-65.424 CenterZ=0 NormalX=0 NormalY=0 NormalZ=1 AngleXU=0 Radius=1
    g314: Circle CenterX=46.0728 CenterY=-69.424 CenterZ=0 NormalX=0 NormalY=0 NormalZ=1 AngleXU=0 Radius=1
    g315: BSplineCurve PolesCount=3 KnotsCount=2 Degree=2 IsPeriodic=0
    g316: GeomPoint X=42.5666 Y=-67.3492 Z=0
    g317: GeomPoint X=46.0728 Y=-69.424 Z=0
    g318: Circle CenterX=46.0728 CenterY=-87.7794 CenterZ=0 NormalX=0 NormalY=0 NormalZ=1 AngleXU=0 Radius=1
    g319: Circle CenterX=46.0728 CenterY=-91.7794 CenterZ=0 NormalX=0 NormalY=0 NormalZ=1 AngleXU=0 Radius=1
    g320: Circle CenterX=42.0728 CenterY=-91.7794 CenterZ=0 NormalX=0 NormalY=0 NormalZ=1 AngleXU=0 Radius=1
    g321: BSplineCurve PolesCount=3 KnotsCount=2 Degree=2 IsPeriodic=0
    g322: GeomPoint X=46.0728 Y=-87.7794 Z=0
    g323: GeomPoint X=42.0728 Y=-91.7794 Z=0
    g324: Circle CenterX=2.07281 CenterY=-91.7794 CenterZ=0 NormalX=0 NormalY=0 NormalZ=1 AngleXU=0 Radius=1
    g325: Circle CenterX=-1.92719 CenterY=-91.7794 CenterZ=0 NormalX=0 NormalY=0 NormalZ=1 AngleXU=0 Radius=1
    g326: Circle CenterX=1.57905 CenterY=-89.8542 CenterZ=0 NormalX=0 NormalY=0 NormalZ=1 AngleXU=0 Radius=1
    g327: BSplineCurve PolesCount=3 KnotsCount=2 Degree=2 IsPeriodic=0
    g328: GeomPoint X=2.07281 Y=-91.7794 Z=0
    g329: GeomPoint X=1.57905 Y=-89.8542 Z=0
    g330: LineSegment StartX=2.07281 StartY=-91.7794 StartZ=0 EndX=42.0728 EndY=-91.7794 EndZ=0
    g331: LineSegment StartX=46.0728 StartY=-87.7794 StartZ=0 EndX=46.0728 EndY=-69.424 EndZ=0
    g332: LineSegment StartX=42.5666 StartY=-67.3492 StartZ=0 EndX=1.57905 EndY=-89.8542 EndZ=0
    g333: Circle CenterX=322.073 CenterY=76.4095 CenterZ=0 NormalX=0 NormalY=0 NormalZ=1 AngleXU=0 Radius=4
    g334: BSplineCurve PolesCount=3 KnotsCount=2 Degree=2 IsPeriodic=0
    g335: GeomPoint X=318.073 Y=72.4095 Z=0
    g336: GeomPoint X=322.073 Y=76.4095 Z=0
    g337: Circle CenterX=375.073 CenterY=72.4095 CenterZ=0 NormalX=0 NormalY=0 NormalZ=1 AngleXU=0 Radius=1
    g338: Circle CenterX=375.073 CenterY=76.4095 CenterZ=0 NormalX=0 NormalY=0 NormalZ=1 AngleXU=0 Radius=1
    g339: Circle CenterX=371.073 CenterY=76.4095 CenterZ=0 NormalX=0 NormalY=0 NormalZ=1 AngleXU=0 Radius=1
    g340: BSplineCurve PolesCount=3 KnotsCount=2 Degree=2 IsPeriodic=0
    g341: GeomPoint X=375.073 Y=72.4095 Z=0
    g342: GeomPoint X=371.073 Y=76.4095 Z=0
    g343: LineSegment StartX=322.073 StartY=76.4095 StartZ=0 EndX=371.073 EndY=76.4095 EndZ=0
    g344: LineSegment StartX=318.073 StartY=72.4095 StartZ=0 EndX=318.073 EndY=-47.4805 EndZ=0
    g345: LineSegment StartX=375.073 StartY=72.4095 StartZ=0 EndX=375.073 EndY=-78.7896 EndZ=0
    g346: ArcOfCircle CenterX=-26.9272 CenterY=22.1087 CenterZ=0 NormalX=0 NormalY=0 NormalZ=1 AngleXU=0 Radius=4 StartAngle=5e-16 EndAngle=3.14159
    g347: LineSegment StartX=-30.9272 StartY=22.1087 StartZ=0 EndX=-34.9272 EndY=-83.7794 EndZ=0
    g348: LineSegment StartX=-18.9272 StartY=-83.7794 StartZ=0 EndX=-22.9272 EndY=22.1087 EndZ=0
  constraints (572):
    c: Coincident(g0,g2)
    c: Block(g0)
    c: Block(g1)
    c: Vertical(g3)
    c: Vertical(g4)
    c: Block(g4)
    c: Block(g3)
    c: Tangent(g6,g7) = 1.5708
    c: Tangent(g7,g9) = 1.5708
    c: Equal(g6,g9)
    c: Coincident(g8,g6)
    c: Coincident(g8,g9)
    c: Block(g7)
    c: Block(g8)
    c: Weight(g10) = 1
    c: Equal(g10,g11)
    c: Equal(g10,g12)
    c: InternalAlignment(g10,g13)
    c: InternalAlignment(g11,g13)
    c: InternalAlignment(g12,g13)
    c: InternalAlignment(g14,g13)
    c: InternalAlignment(g15,g13)
    c: Weight(g16) = 1
    c: Equal(g16,g17)
    c: Equal(g16,g18)
    c: InternalAlignment(g16,g19)
    c: InternalAlignment(g17,g19)
    c: InternalAlignment(g18,g19)
    c: InternalAlignment(g20,g19)
    c: InternalAlignment(g21,g19)
    c: Block(g19)
    c: Block(g13)
    c: Weight(g22) = 1
    c: Equal(g22,g23)
    c: Equal(g22,g24)
    c: InternalAlignment(g22,g25)
    c: InternalAlignment(g23,g25)
    c: InternalAlignment(g24,g25)
    c: InternalAlignment(g26,g25)
    c: InternalAlignment(g27,g25)
    c: Weight(g28) = 1
    c: Equal(g28,g29)
    c: Equal(g28,g30)
    c: InternalAlignment(g28,g31)
    c: InternalAlignment(g29,g31)
    c: InternalAlignment(g30,g31)
    c: InternalAlignment(g32,g31)
    c: InternalAlignment(g33,g31)
    c: Block(g31)
    c: Block(g25)
    c: Weight(g34) = 1
    c: Equal(g34,g35)
    c: Equal(g34,g36)
    c: InternalAlignment(g34,g37)
    c: InternalAlignment(g35,g37)
    c: InternalAlignment(g36,g37)
    c: InternalAlignment(g38,g37)
    c: InternalAlignment(g39,g37)
    c: Weight(g40) = 1
    c: Equal(g40,g41)
    c: Equal(g40,g42)
    c: InternalAlignment(g40,g43)
    c: InternalAlignment(g41,g43)
    c: InternalAlignment(g42,g43)
    c: InternalAlignment(g44,g43)
    c: InternalAlignment(g45,g43)
    c: Block(g37)
    c: Block(g43)
    c: Coincident(g46,g4)
    c: Coincident(g46,g3)
    c: Horizontal(g46)
    c: Distance(g46) = 450
    c: Coincident(g47,g4)
    c: Coincident(g47,g3)
    c: Horizontal(g47)
    c: Horizontal(g48)
    c: Coincident(g2,g48)
    c: Block(g48)
    c: Coincident(g1,g48)
    c: Weight(g49) = 1
    c: Equal(g49,g50)
    c: Equal(g49,g51)
    c: InternalAlignment(g49,g52)
    c: InternalAlignment(g50,g52)
    c: InternalAlignment(g51,g52)
    c: InternalAlignment(g53,g52)
    c: InternalAlignment(g54,g52)
    c: Block(g52)
    c: Weight(g55) = 1
    c: Equal(g55,g56)
    c: Equal(g55,g57)
    c: InternalAlignment(g55,g58)
    c: InternalAlignment(g56,g58)
    c: InternalAlignment(g57,g58)
    c: InternalAlignment(g59,g58)
    c: InternalAlignment(g60,g58)
    c: Block(g58)
    c: Weight(g61) = 1
    c: Equal(g61,g62)
    c: Equal(g61,g63)
    c: InternalAlignment(g61,g64)
    c: InternalAlignment(g62,g64)
    c: InternalAlignment(g63,g64)
    c: InternalAlignment(g65,g64)
    c: InternalAlignment(g66,g64)
    c: Block(g64)
    c: Weight(g67) = 1
    c: Equal(g67,g68)
    c: Equal(g67,g69)
    c: InternalAlignment(g67,g70)
    c: InternalAlignment(g68,g70)
    c: InternalAlignment(g69,g70)
    c: InternalAlignment(g71,g70)
    c: InternalAlignment(g72,g70)
    c: Block(g70)
    c: Weight(g73) = 1
    c: Equal(g73,g74)
    c: Equal(g73,g75)
    c: InternalAlignment(g73,g76)
    c: InternalAlignment(g74,g76)
    c: InternalAlignment(g75,g76)
    c: InternalAlignment(g77,g76)
    c: InternalAlignment(g78,g76)
    c: Weight(g79) = 1
    c: Equal(g79,g80)
    c: Equal(g79,g81)
    c: InternalAlignment(g79,g82)
    c: InternalAlignment(g80,g82)
    c: InternalAlignment(g81,g82)
    c: InternalAlignment(g83,g82)
    c: InternalAlignment(g84,g82)
    c: Block(g76)
    c: Block(g82)
    c: Coincident(g85,g76)
    c: Coincident(g85,g82)
    c: Vertical(g85)
    c: Coincident(g86,g76)
    c: Coincident(g86,g58)
    c: Coincident(g87,g58)
    c: Coincident(g87,g82)
    c: Weight(g88) = 1
    c: Equal(g88,g89)
    c: Equal(g88,g90)
    c: InternalAlignment(g88,g91)
    c: InternalAlignment(g89,g91)
    c: InternalAlignment(g90,g91)
    c: InternalAlignment(g92,g91)
    c: InternalAlignment(g93,g91)
    c: Weight(g94) = 1
    c: Equal(g94,g95)
    c: Equal(g94,g96)
    c: InternalAlignment(g94,g97)
    c: InternalAlignment(g95,g97)
    c: InternalAlignment(g96,g97)
    c: InternalAlignment(g98,g97)
    c: InternalAlignment(g99,g97)
    c: Block(g91)
    c: Block(g97)
    c: Coincident(g100,g91)
    c: Coincident(g100,g97)
    c: Vertical(g100)
    c: Coincident(g101,g91)
    c: Coincident(g101,g52)
    c: Coincident(g102,g52)
    c: Coincident(g102,g97)
    c: Weight(g103) = 1
    c: Equal(g103,g104)
    c: Equal(g103,g105)
    c: InternalAlignment(g103,g106)
    c: InternalAlignment(g104,g106)
    c: InternalAlignment(g105,g106)
    c: InternalAlignment(g107,g106)
    c: InternalAlignment(g108,g106)
    c: Weight(g109) = 1
    c: Equal(g109,g110)
    c: Equal(g109,g111)
    c: InternalAlignment(g109,g112)
    c: InternalAlignment(g110,g112)
    c: InternalAlignment(g111,g112)
    c: InternalAlignment(g113,g112)
    c: InternalAlignment(g114,g112)
    c: Block(g106)
    c: Block(g112)
    c: Coincident(g115,g106)
    c: Coincident(g115,g112)
    c: Vertical(g115)
    c: Coincident(g116,g112)
    c: Coincident(g116,g70)
    c: Coincident(g117,g70)
    c: Coincident(g117,g106)
    c: Weight(g118) = 1
    c: Equal(g118,g119)
    c: Equal(g118,g120)
    c: InternalAlignment(g118,g121)
    c: InternalAlignment(g119,g121)
    c: InternalAlignment(g120,g121)
    c: InternalAlignment(g122,g121)
    c: InternalAlignment(g123,g121)
    c: Weight(g124) = 1
    c: Equal(g124,g125)
    c: Equal(g124,g126)
    c: InternalAlignment(g124,g127)
    c: InternalAlignment(g125,g127)
    c: InternalAlignment(g126,g127)
    c: InternalAlignment(g128,g127)
    c: InternalAlignment(g129,g127)
    c: Block(g121)
    c: Block(g127)
    c: Coincident(g130,g121)
    c: Coincident(g130,g127)
    c: Vertical(g130)
    c: Coincident(g131,g127)
    c: Coincident(g131,g64)
    c: Coincident(g132,g64)
    c: Coincident(g132,g121)
    c: Weight(g133) = 1
    c: Equal(g133,g134)
    c: Equal(g133,g135)
    c: InternalAlignment(g133,g136)
    c: InternalAlignment(g134,g136)
    c: InternalAlignment(g135,g136)
    c: InternalAlignment(g137,g136)
    c: InternalAlignment(g138,g136)
    c: Weight(g139) = 1
    c: Equal(g139,g140)
    c: Equal(g139,g141)
    c: InternalAlignment(g139,g142)
    c: InternalAlignment(g140,g142)
    c: InternalAlignment(g141,g142)
    c: InternalAlignment(g143,g142)
    c: InternalAlignment(g144,g142)
    c: Weight(g145) = 1
    c: Equal(g145,g146)
    c: Equal(g145,g147)
    c: InternalAlignment(g145,g148)
    c: InternalAlignment(g146,g148)
    c: InternalAlignment(g147,g148)
    c: InternalAlignment(g149,g148)
    c: InternalAlignment(g150,g148)
    c: Weight(g151) = 1
    c: Equal(g151,g152)
    c: Equal(g151,g153)
    c: InternalAlignment(g151,g154)
    c: InternalAlignment(g152,g154)
    c: InternalAlignment(g153,g154)
    c: InternalAlignment(g155,g154)
    c: InternalAlignment(g156,g154)
    c: Block(g154)
    c: Block(g148)
    c: Block(g142)
    c: Block(g136)
    c: Coincident(g157,g31)
    c: Coincident(g157,g154)
    c: Coincident(g158,g154)
    c: Coincident(g158,g148)
    c: Horizontal(g158)
    c: Coincident(g159,g148)
    c: Coincident(g159,g31)
    c: Vertical(g159)
    c: Coincident(g160,g25)
    c: Coincident(g160,g142)
    c: Vertical(g160)
    c: Coincident(g161,g142)
    c: Coincident(g161,g136)
    c: Horizontal(g161)
    c: Coincident(g162,g136)
    c: Coincident(g162,g25)
    c: Weight(g163) = 1
    c: Equal(g163,g164)
    c: Equal(g163,g165)
    c: InternalAlignment(g163,g166)
    c: InternalAlignment(g164,g166)
    c: InternalAlignment(g165,g166)
    c: InternalAlignment(g167,g166)
    c: InternalAlignment(g168,g166)
    c: Weight(g169) = 1
    c: Equal(g169,g170)
    c: Equal(g169,g171)
    c: InternalAlignment(g169,g172)
    c: InternalAlignment(g170,g172)
    c: InternalAlignment(g171,g172)
    c: InternalAlignment(g173,g172)
    c: InternalAlignment(g174,g172)
    c: Weight(g175) = 1
    c: Equal(g175,g176)
    c: Equal(g175,g177)
    c: InternalAlignment(g175,g178)
    c: InternalAlignment(g176,g178)
    c: InternalAlignment(g177,g178)
    c: InternalAlignment(g179,g178)
    c: InternalAlignment(g180,g178)
    c: Weight(g181) = 1
    c: Equal(g181,g182)
    c: Equal(g181,g183)
    c: InternalAlignment(g181,g184)
    c: InternalAlignment(g182,g184)
    c: InternalAlignment(g183,g184)
    c: InternalAlignment(g185,g184)
    c: InternalAlignment(g186,g184)
    c: Block(g184)
    c: Block(g178)
    c: Block(g172)
    c: Block(g166)
    c: Coincident(g187,g184)
    c: Coincident(g187,g178)
    c: Horizontal(g187)
    c: Coincident(g188,g178)
    c: Coincident(g188,g13)
    c: Vertical(g188)
    c: Coincident(g189,g19)
    c: Coincident(g189,g172)
    c: Vertical(g189)
    c: Coincident(g190,g172)
    c: Coincident(g190,g166)
    c: Horizontal(g190)
    c: Coincident(g191,g166)
    c: Coincident(g191,g19)
    c: Coincident(g192,g13)
    c: Weight(g193) = 1
    c: Equal(g193,g194)
    c: Equal(g193,g195)
    c: InternalAlignment(g193,g196)
    c: InternalAlignment(g194,g196)
    c: InternalAlignment(g195,g196)
    c: InternalAlignment(g197,g196)
    c: InternalAlignment(g198,g196)
    c: Weight(g199) = 1
    c: Equal(g199,g200)
    c: Equal(g199,g201)
    c: InternalAlignment(g199,g202)
    c: InternalAlignment(g200,g202)
    c: InternalAlignment(g201,g202)
    c: InternalAlignment(g203,g202)
    c: InternalAlignment(g204,g202)
    c: Block(g202)
    c: Block(g196)
    c: Coincident(g205,g202)
    c: Coincident(g205,g37)
    c: Coincident(g206,g37)
    c: Coincident(g206,g196)
    c: Coincident(g207,g196)
    c: Coincident(g207,g202)
    c: Vertical(g207)
    c: Weight(g208) = 1
    c: Equal(g208,g209)
    c: Equal(g208,g210)
    c: InternalAlignment(g208,g211)
    c: InternalAlignment(g209,g211)
    c: InternalAlignment(g210,g211)
    c: InternalAlignment(g212,g211)
    c: InternalAlignment(g213,g211)
    c: Weight(g214) = 1
    c: Equal(g214,g215)
    c: Equal(g214,g216)
    c: InternalAlignment(g214,g217)
    c: InternalAlignment(g215,g217)
    c: InternalAlignment(g216,g217)
    c: InternalAlignment(g218,g217)
    c: InternalAlignment(g219,g217)
    c: Block(g217)
    c: Block(g211)
    c: Coincident(g220,g211)
    c: Coincident(g220,g43)
    c: Coincident(g221,g43)
    c: Coincident(g221,g217)
    c: Coincident(g222,g217)
    c: Coincident(g222,g211)
    c: Vertical(g222)
    c: Horizontal(g223)
    c: Block(g223)
    c: Vertical(g224)
    c: Block(g224)
    c: Block(g225)
    c: Weight(g226) = 1
    c: Equal(g226,g227)
    c: Equal(g226,g228)
    c: InternalAlignment(g226,g229)
    c: InternalAlignment(g227,g229)
    c: InternalAlignment(g228,g229)
    c: InternalAlignment(g230,g229)
    c: InternalAlignment(g231,g229)
    c: Weight(g232) = 1
    c: Equal(g232,g233)
    c: Equal(g232,g234)
    c: InternalAlignment(g232,g235)
    c: InternalAlignment(g233,g235)
    c: InternalAlignment(g234,g235)
    c: InternalAlignment(g236,g235)
    c: InternalAlignment(g237,g235)
    c: Weight(g238) = 1
    c: Equal(g238,g239)
    c: Equal(g238,g240)
    c: InternalAlignment(g238,g241)
    c: InternalAlignment(g239,g241)
    c: InternalAlignment(g240,g241)
    c: InternalAlignment(g242,g241)
    c: InternalAlignment(g243,g241)
    c: Weight(g244) = 1
    c: Equal(g244,g245)
    c: Equal(g244,g246)
    c: InternalAlignment(g244,g247)
    c: InternalAlignment(g245,g247)
    c: InternalAlignment(g246,g247)
    c: InternalAlignment(g248,g247)
    c: InternalAlignment(g249,g247)
    c: Block(g229)
    c: Block(g235)
    c: Block(g241)
    c: Block(g247)
    c: Coincident(g250,g235)
    c: Coincident(g250,g229)
    c: Horizontal(g250)
    c: Block(g192)
    c: Weight(g251) = 1
    c: Equal(g251,g252)
    c: Equal(g251,g253)
    c: InternalAlignment(g251,g254)
    c: InternalAlignment(g252,g254)
    c: InternalAlignment(g253,g254)
    c: InternalAlignment(g255,g254)
    c: InternalAlignment(g256,g254)
    c: Weight(g257) = 1
    c: Equal(g257,g258)
    c: Equal(g257,g259)
    c: InternalAlignment(g257,g260)
    c: InternalAlignment(g258,g260)
    c: InternalAlignment(g259,g260)
    c: InternalAlignment(g261,g260)
    c: InternalAlignment(g262,g260)
    c: Block(g254)
    c: Block(g260)
    c: Coincident(g263,g254)
    c: Coincident(g263,g260)
    c: Weight(g264) = 1
    c: Equal(g264,g265)
    c: Equal(g264,g266)
    c: InternalAlignment(g264,g267)
    c: InternalAlignment(g265,g267)
    c: InternalAlignment(g266,g267)
    c: InternalAlignment(g268,g267)
    c: InternalAlignment(g269,g267)
    c: Weight(g270) = 1
    c: Equal(g270,g271)
    c: Equal(g270,g272)
    c: InternalAlignment(g270,g273)
    c: InternalAlignment(g271,g273)
    c: InternalAlignment(g272,g273)
    c: InternalAlignment(g274,g273)
    c: InternalAlignment(g275,g273)
    c: Weight(g276) = 1
    c: Equal(g276,g277)
    c: Equal(g276,g278)
    c: InternalAlignment(g276,g279)
    c: InternalAlignment(g277,g279)
    c: InternalAlignment(g278,g279)
    c: InternalAlignment(g280,g279)
    c: InternalAlignment(g281,g279)
    c: Block(g279)
    c: Block(g273)
    c: Block(g267)
    c: Coincident(g282,g273)
    c: Coincident(g282,g267)
    c: Coincident(g283,g267)
    c: Coincident(g283,g279)
    c: Vertical(g283)
    c: Coincident(g284,g279)
    c: Coincident(g284,g273)
    c: Horizontal(g284)
    c: Weight(g285) = 1
    c: Equal(g285,g286)
    c: InternalAlignment(g285,g287)
    c: InternalAlignment(g286,g287)
    c: InternalAlignment(g288,g287)
    c: InternalAlignment(g289,g287)
    c: Weight(g290) = 1
    c: InternalAlignment(g291,g293)
    c: InternalAlignment(g292,g293)
    c: InternalAlignment(g294,g293)
    c: InternalAlignment(g295,g293)
    c: Weight(g296) = 1
    c: Equal(g296,g297)
    c: Equal(g296,g298)
    c: InternalAlignment(g296,g299)
    c: InternalAlignment(g297,g299)
    c: InternalAlignment(g298,g299)
    c: InternalAlignment(g300,g299)
    c: InternalAlignment(g301,g299)
    c: Equal(g302,g303)
    c: Equal(g302,g304)
    c: InternalAlignment(g302,g305)
    c: InternalAlignment(g303,g305)
    c: InternalAlignment(g304,g305)
    c: InternalAlignment(g306,g305)
    c: InternalAlignment(g307,g305)
    c: Block(g293)
    c: Block(g299)
    c: Block(g305)
    c: Block(g287)
    c: Coincident(g308,g287)
    c: Coincident(g308,g293)
    c: Horizontal(g308)
    c: Coincident(g309,g293)
    c: Coincident(g309,g299)
    c: Vertical(g309)
    c: Coincident(g310,g299)
    c: Coincident(g310,g305)
    c: Horizontal(g310)
    c: Coincident(g311,g305)
    c: Coincident(g311,g287)
    c: Weight(g312) = 1
    c: Equal(g312,g313)
    c: Equal(g312,g314)
    c: InternalAlignment(g312,g315)
    c: InternalAlignment(g313,g315)
    c: InternalAlignment(g314,g315)
    c: InternalAlignment(g316,g315)
    c: InternalAlignment(g317,g315)
    c: Weight(g318) = 1
    c: Equal(g318,g319)
    c: Equal(g318,g320)
    c: InternalAlignment(g318,g321)
    c: InternalAlignment(g319,g321)
    c: InternalAlignment(g320,g321)
    c: InternalAlignment(g322,g321)
    c: InternalAlignment(g323,g321)
    c: Weight(g324) = 1
    c: Equal(g324,g325)
    c: Equal(g324,g326)
    c: InternalAlignment(g324,g327)
    c: InternalAlignment(g325,g327)
    c: InternalAlignment(g326,g327)
    c: InternalAlignment(g328,g327)
    c: InternalAlignment(g329,g327)
    c: Block(g327)
    c: Block(g321)
    c: Block(g315)
    c: Coincident(g330,g327)
    c: Coincident(g330,g321)
    c: Horizontal(g330)
    c: Coincident(g331,g321)
    c: Coincident(g331,g315)
    c: Vertical(g331)
    c: Coincident(g332,g315)
    c: Coincident(g332,g327)
    c: InternalAlignment(g333,g334)
    c: InternalAlignment(g335,g334)
    c: InternalAlignment(g336,g334)
    c: Block(g334)
    c: Equal(g337,g338)
    c: Equal(g337,g339)
    c: InternalAlignment(g337,g340)
    c: InternalAlignment(g338,g340)
    c: InternalAlignment(g339,g340)
    c: InternalAlignment(g341,g340)
    c: InternalAlignment(g342,g340)
    c: Block(g340)
    c: Coincident(g343,g334)
    c: Horizontal(g343)
    c: Block(g343)
    c: Coincident(g344,g334)
    c: Coincident(g344,g260)
    c: Vertical(g344)
    c: Coincident(g345,g340)
    c: Coincident(g345,g254)
    c: Vertical(g345)
    c: Coincident(g347,g5)
    c: Coincident(g348,g5)
    c: Block(g346)
    c: Block(g5)
    c: Block(g348)
    c: Block(g347)
    c: Distance(g344) = 119.89
FEATURE [Sketcher::SketchObject] Sketch001
  FullyConstrained = true
  MapMode = 4
  Placement = pos=(0,0,0) rot=(0.57735,0.57735,0.57735;2.0944rad)
  Support = -> [Sketch]
  sketch-geometry (46):
    g0: BSplineCurve PolesCount=3 KnotsCount=2 Degree=2 IsPeriodic=0
    g1: ArcOfCircle CenterX=73.1223 CenterY=-32.291 CenterZ=0 NormalX=0 NormalY=0 NormalZ=1 AngleXU=0 Radius=13 StartAngle=5.92268 EndAngle=9.06428
    g2: ArcOfCircle CenterX=66.7816 CenterY=-49.1439 CenterZ=0 NormalX=0 NormalY=0 NormalZ=1 AngleXU=0 Radius=13 StartAngle=2.78068 EndAngle=5.92131
    g3: ArcOfCircle CenterX=55.9263 CenterY=-78.1807 CenterZ=0 NormalX=0 NormalY=0 NormalZ=1 AngleXU=0 Radius=13 StartAngle=5.92268 EndAngle=9.06428
    g4: ArcOfCircle CenterX=49.5884 CenterY=-95.0342 CenterZ=0 NormalX=0 NormalY=0 NormalZ=1 AngleXU=0 Radius=13 StartAngle=2.78068 EndAngle=5.92131
    g5: ArcOfCircle CenterX=38.7206 CenterY=-124.067 CenterZ=0 NormalX=0 NormalY=0 NormalZ=1 AngleXU=0 Radius=13 StartAngle=5.92268 EndAngle=9.06428
    g6: ArcOfCircle CenterX=32.3875 CenterY=-140.92 CenterZ=0 NormalX=0 NormalY=0 NormalZ=1 AngleXU=0 Radius=13 StartAngle=2.78068 EndAngle=5.92131
    g7: ArcOfCircle CenterX=21.4715 CenterY=-169.934 CenterZ=0 NormalX=0 NormalY=0 NormalZ=1 AngleXU=0 Radius=13 StartAngle=5.92268 EndAngle=9.06428
    g8: ArcOfCircle CenterX=15.1336 CenterY=-186.787 CenterZ=0 NormalX=0 NormalY=0 NormalZ=1 AngleXU=0 Radius=13 StartAngle=2.78068 EndAngle=5.92131
    g9-g12: Circle x4 (B-spline internal-alignment scaffolding for g13; pole/knot coordinates omitted)
    g13: BSplineCurve PolesCount=4 KnotsCount=2 Degree=3 IsPeriodic=0
    g14: GeomPoint X=28.8094 Y=-19.0875 Z=0
    g15: GeomPoint X=47.0443 Y=-50.4712 Z=0
    g16: Circle CenterX=53.5586 CenterY=-23.2695 CenterZ=0 NormalX=0 NormalY=0 NormalZ=1 AngleXU=0 Radius=3.24518
    g17: Circle CenterX=-195.441 CenterY=-127.082 CenterZ=0 NormalX=0 NormalY=0 NormalZ=1 AngleXU=0 Radius=1
    g18: Circle CenterX=-8.24091 CenterY=-197.481 CenterZ=0 NormalX=0 NormalY=0 NormalZ=1 AngleXU=0 Radius=1
    g19: Circle CenterX=12.8789 CenterY=-141.321 CenterZ=0 NormalX=0 NormalY=0 NormalZ=1 AngleXU=0 Radius=1
    g20: BSplineCurve PolesCount=3 KnotsCount=2 Degree=2 IsPeriodic=0
    g21: GeomPoint X=-195.441 Y=-127.082 Z=0
    g22: GeomPoint X=12.8789 Y=-141.321 Z=0
    g23: Circle CenterX=-12.8016 CenterY=-179.036 CenterZ=0 NormalX=0 NormalY=0 NormalZ=1 AngleXU=0 Radius=10.5072
    g24: Circle CenterX=0.933922 CenterY=-166.43 CenterZ=0 NormalX=0 NormalY=0 NormalZ=1 AngleXU=0 Radius=3.26661
    g25: Circle CenterX=-33.5518 CenterY=-176.44 CenterZ=0 NormalX=0 NormalY=0 NormalZ=1 AngleXU=0 Radius=5.64388
    g26: Circle CenterX=-47.2366 CenterY=-173.859 CenterZ=0 NormalX=0 NormalY=0 NormalZ=1 AngleXU=0 Radius=3.01653
    g27: Circle CenterX=-56.2595 CenterY=-171.456 CenterZ=0 NormalX=0 NormalY=0 NormalZ=1 AngleXU=0 Radius=2.12826
    g28: ArcOfCircle CenterX=51.2151 CenterY=-198.473 CenterZ=0 NormalX=0 NormalY=0 NormalZ=1 AngleXU=0 Radius=20 StartAngle=2.78189 EndAngle=4.35269
    g29: LineSegment StartX=32.4951 StartY=-191.433 StartZ=0 EndX=94.6578 EndY=-26.1352 EndZ=0
    g30: LineSegment StartX=43.1192 StartY=-220.001 StartZ=0 EndX=-196.497 EndY=-129.89 EndZ=0
    g31: LineSegment StartX=43.1192 StartY=-220.001 StartZ=0 EndX=44.1752 EndY=-217.193 EndZ=0
    g32: LineSegment StartX=117.223 StartY=-19.0875 StartZ=0 EndX=117.223 EndY=-16.0875 EndZ=0
    g33: LineSegment StartX=117.223 StartY=-16.0875 StartZ=0 EndX=17.2232 EndY=-16.0875 EndZ=0
    g34: LineSegment StartX=17.2232 StartY=-16.0875 StartZ=0 EndX=17.2232 EndY=-19.0875 EndZ=0
    g35: LineSegment StartX=28.8094 StartY=-19.0875 StartZ=0 EndX=17.2232 EndY=-19.0875 EndZ=0
    g36: LineSegment StartX=47.0443 StartY=-50.4712 StartZ=0 EndX=12.8789 EndY=-141.321 EndZ=0
    g37: LineSegment StartX=-195.441 StartY=-127.082 StartZ=0 EndX=-196.497 EndY=-129.89 EndZ=0
    g38: LineSegment StartX=85.2866 StartY=-36.8766 StartZ=0 EndX=78.9396 EndY=-53.7463 EndZ=0
    g39: LineSegment StartX=60.9579 StartY=-27.7053 StartZ=0 EndX=54.6191 EndY=-44.5532 EndZ=0
    g40: LineSegment StartX=68.0907 StartY=-82.7664 StartZ=0 EndX=61.7465 EndY=-99.6365 EndZ=0
    g41: LineSegment StartX=43.7619 StartY=-73.595 StartZ=0 EndX=37.426 EndY=-90.4435 EndZ=0
    g42: LineSegment StartX=50.885 StartY=-128.652 StartZ=0 EndX=44.5456 EndY=-145.522 EndZ=0
    g43: LineSegment StartX=26.5562 StartY=-119.481 StartZ=0 EndX=20.2251 EndY=-136.329 EndZ=0
    g44: LineSegment StartX=9.3071 StartY=-165.349 StartZ=0 EndX=2.97115 EndY=-182.197 EndZ=0
    g45: LineSegment StartX=33.6358 StartY=-174.52 StartZ=0 EndX=27.2917 EndY=-191.39 EndZ=0
  constraints (71):
    c: Block(g0)
    c: Block(g1)
    c: Block(g2)
    c: Block(g4)
    c: Block(g3)
    c: Block(g6)
    c: Block(g5)
    c: Block(g8)
    c: Block(g7)
    c: Weight(g9) = 1
    c: Equal(g9,g10)
    c: Equal(g9,g11)
    c: Equal(g9,g12)
    c: InternalAlignment(g9-g12 -> g13) x4
    c: InternalAlignment(g14,g13)
    c: InternalAlignment(g15,g13)
    c: Block(g16)
    c: Weight(g17) = 1
    c: Equal(g17,g18)
    c: Equal(g17,g19)
    c: InternalAlignment(g17,g20)
    c: InternalAlignment(g18,g20)
    c: InternalAlignment(g19,g20)
    c: InternalAlignment(g21,g20)
    c: InternalAlignment(g22,g20)
    c: Block(g20)
    c: Block(g23)
    c: Block(g24)
    c: Block(g25)
    c: Block(g26)
    c: Block(g27)
    c: Block(g28)
    c: Coincident(g29,g28)
    c: Coincident(g29,g0)
    c: Block(g13)
    c: Coincident(g31,g30)
    c: Coincident(g31,g28)
    c: Block(g31)
    c: Coincident(g32,g0)
    c: Vertical(g32)
    c: Coincident(g33,g32)
    c: Horizontal(g33)
    c: Coincident(g34,g33)
    c: Vertical(g34)
    c: Block(g33)
    c: Coincident(g35,g13)
    c: Coincident(g35,g34)
    c: Horizontal(g35)
    c: Coincident(g36,g13)
    c: Coincident(g36,g20)
    c: Coincident(g37,g20)
    c: Coincident(g37,g30)
    c: Block(g30)
    c: Coincident(g38,g1)
    c: Coincident(g38,g2)
    c: Coincident(g39,g1)
    c: Coincident(g39,g2)
    c: Coincident(g40,g3)
    c: Coincident(g40,g4)
    c: Coincident(g41,g3)
    c: Coincident(g41,g4)
    c: Coincident(g42,g5)
    c: Coincident(g42,g6)
    c: Coincident(g43,g5)
    c: Coincident(g43,g6)
    c: Coincident(g44,g7)
    c: Coincident(g44,g8)
    c: Coincident(g45,g7)
    c: Coincident(g45,g8)
    c: Distance(g30) = 256
    c: Distance(g33) = 100
FEATURE [Part::Extrusion] Extrude002
  Base = -> Sketch001
  Dir = (1,0,0)
  DirMode = 2
  FaceMakerClass = Part::FaceMakerBullseye
  LengthFwd = 8
  LengthRev = 0
  Solid = true
  Symmetric = false
FEATURE [Sketcher::SketchObject] Sketch002
  FullyConstrained = true
  sketch-geometry (20):
    g0: LineSegment StartX=-2.77179 StartY=-200.304 StartZ=0 EndX=5.22821 EndY=-200.304 EndZ=0
    g1: LineSegment StartX=5.22821 StartY=-200.304 StartZ=0 EndX=5.22821 EndY=-197.304 EndZ=0
    g2: LineSegment StartX=-2.77179 StartY=-200.304 StartZ=0 EndX=-2.77179 EndY=-197.304 EndZ=0
    g3: LineSegment StartX=5.22821 StartY=-197.304 StartZ=0 EndX=8.22821 EndY=-197.304 EndZ=0
    g4: LineSegment StartX=-2.77179 StartY=-197.304 StartZ=0 EndX=-5.77179 EndY=-197.304 EndZ=0
    g5: LineSegment StartX=19.2282 StartY=-203.304 StartZ=0 EndX=19.2282 EndY=-206.304 EndZ=0
    g6: LineSegment StartX=-16.7718 StartY=-203.304 StartZ=0 EndX=-16.7718 EndY=-206.304 EndZ=0
    g7: LineSegment StartX=-16.7718 StartY=-206.304 StartZ=0 EndX=19.2282 EndY=-206.304 EndZ=0
    g8: Circle CenterX=-16.7718 CenterY=-203.304 CenterZ=0 NormalX=0 NormalY=0 NormalZ=1 AngleXU=0 Radius=1
    g9: Circle CenterX=-5.77179 CenterY=-203.304 CenterZ=0 NormalX=0 NormalY=0 NormalZ=1 AngleXU=0 Radius=1
    g10: Circle CenterX=-5.77179 CenterY=-197.304 CenterZ=0 NormalX=0 NormalY=0 NormalZ=1 AngleXU=0 Radius=1
    g11: BSplineCurve PolesCount=3 KnotsCount=2 Degree=2 IsPeriodic=0
    g12: GeomPoint X=-16.7718 Y=-203.304 Z=0
    g13: GeomPoint X=-5.77179 Y=-197.304 Z=0
    g14: Circle CenterX=19.2282 CenterY=-203.304 CenterZ=0 NormalX=0 NormalY=0 NormalZ=1 AngleXU=0 Radius=1
    g15: Circle CenterX=8.22821 CenterY=-203.304 CenterZ=0 NormalX=0 NormalY=0 NormalZ=1 AngleXU=0 Radius=1
    g16: Circle CenterX=8.22821 CenterY=-197.304 CenterZ=0 NormalX=0 NormalY=0 NormalZ=1 AngleXU=0 Radius=1
    g17: BSplineCurve PolesCount=3 KnotsCount=2 Degree=2 IsPeriodic=0
    g18: GeomPoint X=19.2282 Y=-203.304 Z=0
    g19: GeomPoint X=8.22821 Y=-197.304 Z=0
  constraints (41):
    c: Horizontal(g0)
    c: Distance(g0) = 8
    c: Coincident(g1,g0)
    c: Vertical(g1)
    c: Distance(g1) = 3
    c: Coincident(g2,g0)
    c: Vertical(g2)
    c: Distance(g2) = 3
    c: Coincident(g3,g1)
    c: Horizontal(g3)
    c: Distance(g3) = 3
    c: Coincident(g4,g2)
    c: Horizontal(g4)
    c: Distance(g4) = 3
    c: Vertical(g5)
    c: Vertical(g6)
    c: Coincident(g7,g6)
    c: Coincident(g7,g5)
    c: Weight(g8) = 1
    c: Equal(g8,g9)
    c: Equal(g8,g10)
    c: Coincident(g11,g4)
    c: InternalAlignment(g8,g11)
    c: InternalAlignment(g9,g11)
    c: InternalAlignment(g10,g11)
    c: InternalAlignment(g12,g11)
    c: InternalAlignment(g13,g11)
    c: Coincident(g17,g5)
    c: Weight(g14) = 1
    c: Equal(g14,g15)
    c: Equal(g14,g16)
    c: Coincident(g17,g3)
    c: InternalAlignment(g14,g17)
    c: InternalAlignment(g15,g17)
    c: InternalAlignment(g16,g17)
    c: InternalAlignment(g18,g17)
    c: InternalAlignment(g19,g17)
    c: Block(g7)
    c: Block(g17)
    c: Block(g11)
    c: Block(g6)
FEATURE [Part::Extrusion] Extrude003
  Base = -> Sketch002
  Dir = (0,0,1)
  DirMode = 2
  FaceMakerClass = Part::FaceMakerBullseye
  LengthFwd = 260
  LengthRev = 0
  Solid = true
  Symmetric = false
FEATURE [Part::Extrusion] Extrude
  Base = -> Sketch
  Dir = (0,0,1)
  DirMode = 2
  FaceMakerClass = Part::FaceMakerBullseye
  LengthFwd = 14
  LengthRev = 0
  Solid = true
  Symmetric = false
